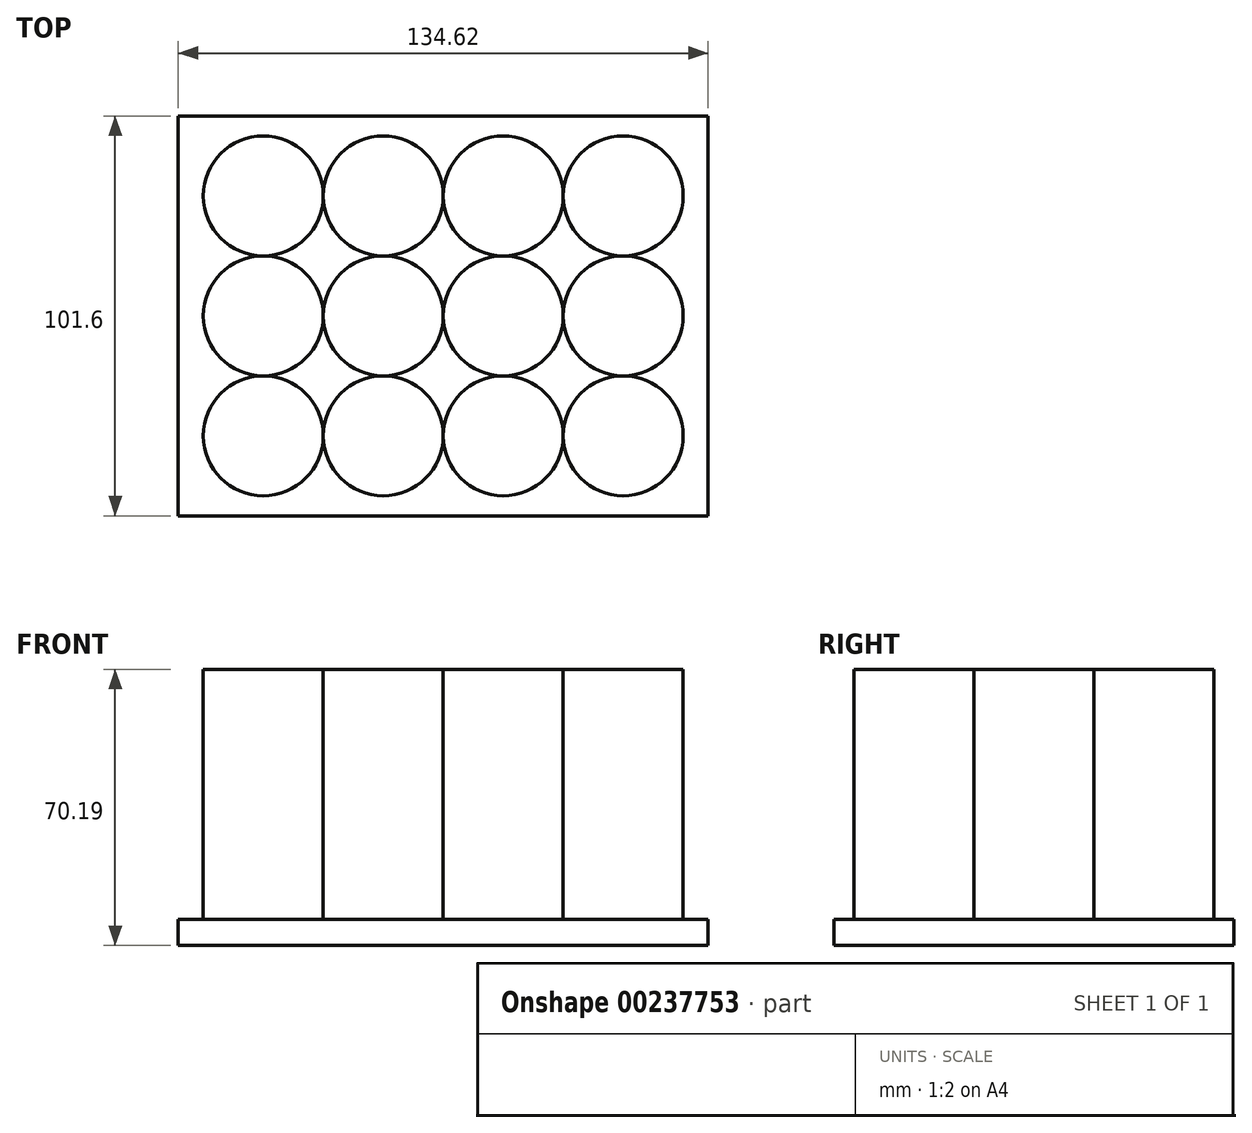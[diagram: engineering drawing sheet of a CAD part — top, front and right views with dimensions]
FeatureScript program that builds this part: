
annotation { "Feature Type Name" : "Feature", "Feature Type Description" : "" }
export const myFeature = defineFeature(function(context is Context, id is Id, definition is map)
    precondition{}
    {
        {
            var Q0;
            Q0=qCreatedBy(makeId("Top.planeOp"),FACE);
            var sketch = newSketch(context, id + "F0", { "sketchPlane" : qUnion([Q0])});
            skCircle(sketch, "E0", {"center": v(-45.72, -30.48) * mm, "radius": 15.24 * mm});
            skCircle(sketch, "E1", {"center": v(-15.24, -30.48) * mm, "radius": 15.24 * mm});
            skCircle(sketch, "E2", {"center": v(15.24, -30.48) * mm, "radius": 15.24 * mm});
            skCircle(sketch, "E3", {"center": v(-45.72, 0) * mm, "radius": 15.24 * mm});
            skCircle(sketch, "E4", {"center": v(-15.24, 0) * mm, "radius": 15.24 * mm});
            skCircle(sketch, "E5", {"center": v(15.24, 0) * mm, "radius": 15.24 * mm});
            skLineSegment(sketch, "E6", {"start": v(-45.72, 0) * mm, "end": v(-45.72, -30.48) * mm, "construction": true});
            skCircle(sketch, "E7", {"center": v(-45.72, 30.48) * mm, "radius": 15.24 * mm});
            skCircle(sketch, "E8", {"center": v(-15.24, 30.48) * mm, "radius": 15.24 * mm});
            skCircle(sketch, "E9", {"center": v(15.24, 30.48) * mm, "radius": 15.24 * mm});
            skLineSegment(sketch, "E10", {"start": v(-45.72, 30.48) * mm, "end": v(-45.72, 0) * mm, "construction": true});
            skCircle(sketch, "E11", {"center": v(45.72, -30.48) * mm, "radius": 15.24 * mm});
            skCircle(sketch, "E12", {"center": v(45.72, 0) * mm, "radius": 15.24 * mm});
            skCircle(sketch, "E13", {"center": v(45.72, 30.48) * mm, "radius": 15.24 * mm});
            skLineSegment(sketch, "E14", {"start": v(45.72, 30.48) * mm, "end": v(45.72, -30.48) * mm, "construction": true});
            skLineSegment(sketch, "E15", {"start": v(-45.72, 0) * mm, "end": v(45.72, 0) * mm, "construction": true});
            skLineSegment(sketch, "E16", {"start": v(-45.72, 30.48) * mm, "end": v(45.72, 30.48) * mm, "construction": true});
            skLineSegment(sketch, "E17", {"start": v(-45.72, -30.48) * mm, "end": v(45.72, -30.48) * mm, "construction": true});
            skSolve(sketch);
        }
        {
            var Q0;
            {var subQ0=sQuery(id+"F0.wireOp",EDGE,"ICpDPUjX-ivMe-23Ei-ieje-qIsjfVPonkm3");var subQ1=makeQuery(id+"F0.imprint","INTERSECT",VERTEX,{"derivedFrom":[subQ0,sQuery(id+"F0.wireOp",EDGE,"1585de0c-b4fc-4455-9636-1ccd38715f07")]});Q0=makeQuery(id+"F0.imprint","IMPRINT",FACE,{"disambiguationData":[TD([[makeQuery(id+"F0.imprint","IMPRINT",EDGE,{"disambiguationData":[TD([[subQ1,-1.0]])],"derivedFrom":subQ0}),1.0]])]});}
            var Q1;
            {var subQ0=sQuery(id+"F0.wireOp",EDGE,"1585de0c-b4fc-4455-9636-1ccd38715f07");var subQ1=makeQuery(id+"F0.imprint","INTERSECT",VERTEX,{"derivedFrom":[sQuery(id+"F0.wireOp",EDGE,"ICpDPUjX-ivMe-23Ei-ieje-qIsjfVPonkm3"),subQ0]});Q1=makeQuery(id+"F0.imprint","IMPRINT",FACE,{"disambiguationData":[TD([[makeQuery(id+"F0.imprint","IMPRINT",EDGE,{"disambiguationData":[TD([[subQ1,1.0]])],"derivedFrom":subQ0}),1.0]])]});}
            var Q2;
            {var subQ0=sQuery(id+"F0.wireOp",EDGE,"8cf919d0-c88a-4376-973f-18324e1bfcb2");var subQ1=makeQuery(id+"F0.imprint","INTERSECT",VERTEX,{"derivedFrom":[sQuery(id+"F0.wireOp",EDGE,"1585de0c-b4fc-4455-9636-1ccd38715f07"),subQ0]});Q2=makeQuery(id+"F0.imprint","IMPRINT",FACE,{"disambiguationData":[TD([[makeQuery(id+"F0.imprint","IMPRINT",EDGE,{"disambiguationData":[TD([[subQ1,-1.0]])],"derivedFrom":subQ0}),1.0]])]});}
            var Q3;
            {var subQ0=sQuery(id+"F0.wireOp",EDGE,"0c448a11-c32a-4d7b-bc3d-f4b18554e8e6");var subQ1=makeQuery(id+"F0.imprint","INTERSECT",VERTEX,{"derivedFrom":[sQuery(id+"F0.wireOp",EDGE,"8cf919d0-c88a-4376-973f-18324e1bfcb2"),subQ0]});Q3=makeQuery(id+"F0.imprint","IMPRINT",FACE,{"disambiguationData":[TD([[makeQuery(id+"F0.imprint","IMPRINT",EDGE,{"disambiguationData":[TD([[subQ1,-1.0]])],"derivedFrom":subQ0}),1.0]])]});}
            var Q4;
            {var subQ0=sQuery(id+"F0.wireOp",EDGE,"877ee094-fdc9-495d-ab0e-c5a52c05f9cd");var subQ4=makeQuery(id+"F0.imprint","INTERSECT",VERTEX,{"derivedFrom":[sQuery(id+"F0.wireOp",EDGE,"8cf919d0-c88a-4376-973f-18324e1bfcb2"),subQ0]});Q4=makeQuery(id+"F0.imprint","IMPRINT",FACE,{"disambiguationData":[TD([[makeQuery(id+"F0.imprint","IMPRINT",EDGE,{"disambiguationData":[TD([[subQ4,1.0]])],"derivedFrom":subQ0}),1.0]])]});}
            var Q5;
            {var subQ0=sQuery(id+"F0.wireOp",EDGE,"d8245553-00ec-417b-91d8-0db8256ae251");var subQ4=makeQuery(id+"F0.imprint","INTERSECT",VERTEX,{"derivedFrom":[sQuery(id+"F0.wireOp",EDGE,"1585de0c-b4fc-4455-9636-1ccd38715f07"),subQ0]});Q5=makeQuery(id+"F0.imprint","IMPRINT",FACE,{"disambiguationData":[TD([[makeQuery(id+"F0.imprint","IMPRINT",EDGE,{"disambiguationData":[TD([[subQ4,1.0]])],"derivedFrom":subQ0}),1.0]])]});}
            var Q6;
            {var subQ0=sQuery(id+"F0.wireOp",EDGE,"E0");var subQ1=makeQuery(id+"F0.imprint","INTERSECT",VERTEX,{"derivedFrom":[sQuery(id+"F0.wireOp",EDGE,"d8245553-00ec-417b-91d8-0db8256ae251"),subQ0]});Q6=makeQuery(id+"F0.imprint","IMPRINT",FACE,{"disambiguationData":[TD([[makeQuery(id+"F0.imprint","IMPRINT",EDGE,{"disambiguationData":[TD([[subQ1,1.0]])],"derivedFrom":subQ0}),1.0]])]});}
            var Q7;
            {var subQ0=sQuery(id+"F0.wireOp",EDGE,"E1");var subQ1=makeQuery(id+"F0.imprint","INTERSECT",VERTEX,{"derivedFrom":[subQ0,sQuery(id+"F0.wireOp",EDGE,"E2")]});Q7=makeQuery(id+"F0.imprint","IMPRINT",FACE,{"disambiguationData":[TD([[makeQuery(id+"F0.imprint","IMPRINT",EDGE,{"disambiguationData":[TD([[subQ1,-1.0]])],"derivedFrom":subQ0}),1.0]])]});}
            var Q8;
            {var subQ0=sQuery(id+"F0.wireOp",EDGE,"E2");var subQ1=makeQuery(id+"F0.imprint","INTERSECT",VERTEX,{"derivedFrom":[sQuery(id+"F0.wireOp",EDGE,"0c448a11-c32a-4d7b-bc3d-f4b18554e8e6"),subQ0]});Q8=makeQuery(id+"F0.imprint","IMPRINT",FACE,{"disambiguationData":[TD([[makeQuery(id+"F0.imprint","IMPRINT",EDGE,{"disambiguationData":[TD([[subQ1,-1.0]])],"derivedFrom":subQ0}),1.0]])]});}
            var Q9;
            {var subQ0=sQuery(id+"F0.wireOp",EDGE,"E3");var subQ1=makeQuery(id+"F0.imprint","INTERSECT",VERTEX,{"derivedFrom":[sQuery(id+"F0.wireOp",EDGE,"E0"),subQ0]});Q9=makeQuery(id+"F0.imprint","IMPRINT",FACE,{"disambiguationData":[TD([[makeQuery(id+"F0.imprint","IMPRINT",EDGE,{"disambiguationData":[TD([[subQ1,1.0]])],"derivedFrom":subQ0}),1.0]])]});}
            var Q10;
            {var subQ0=sQuery(id+"F0.wireOp",EDGE,"E4");var subQ1=makeQuery(id+"F0.imprint","INTERSECT",VERTEX,{"derivedFrom":[sQuery(id+"F0.wireOp",EDGE,"E3"),subQ0]});Q10=makeQuery(id+"F0.imprint","IMPRINT",FACE,{"disambiguationData":[TD([[makeQuery(id+"F0.imprint","IMPRINT",EDGE,{"disambiguationData":[TD([[subQ1,1.0]])],"derivedFrom":subQ0}),1.0]])]});}
            var Q11;
            {var subQ0=sQuery(id+"F0.wireOp",EDGE,"E5");var subQ1=makeQuery(id+"F0.imprint","INTERSECT",VERTEX,{"derivedFrom":[sQuery(id+"F0.wireOp",EDGE,"E2"),subQ0]});Q11=makeQuery(id+"F0.imprint","IMPRINT",FACE,{"disambiguationData":[TD([[makeQuery(id+"F0.imprint","IMPRINT",EDGE,{"disambiguationData":[TD([[subQ1,1.0]])],"derivedFrom":subQ0}),1.0]])]});}
            var Q12;
            Q12=makeQuery(id+"F0.imprint","IMPRINT",FACE,{"disambiguationData":[TD([[makeQuery(id+"F0.imprint","IMPRINT",EDGE,{"derivedFrom":sQuery(id+"F0.wireOp",EDGE,"E13")}),1.0]])]});
            var Q13;
            {var subQ0=sQuery(id+"F0.wireOp",EDGE,"E11");var subQ1=makeQuery(id+"F0.imprint","INTERSECT",VERTEX,{"derivedFrom":[sQuery(id+"F0.wireOp",EDGE,"E2"),subQ0]});Q13=makeQuery(id+"F0.imprint","IMPRINT",FACE,{"disambiguationData":[TD([[makeQuery(id+"F0.imprint","IMPRINT",EDGE,{"disambiguationData":[TD([[subQ1,1.0]])],"derivedFrom":subQ0}),1.0]])]});}
            var Q14;
            {var subQ0=sQuery(id+"F0.wireOp",EDGE,"E8");var subQ1=makeQuery(id+"F0.imprint","INTERSECT",VERTEX,{"derivedFrom":[sQuery(id+"F0.wireOp",EDGE,"E7"),subQ0]});Q14=makeQuery(id+"F0.imprint","IMPRINT",FACE,{"disambiguationData":[TD([[makeQuery(id+"F0.imprint","IMPRINT",EDGE,{"disambiguationData":[TD([[subQ1,1.0]])],"derivedFrom":subQ0}),1.0]])]});}
            var Q15;
            {var subQ0=sQuery(id+"F0.wireOp",EDGE,"E7");var subQ1=makeQuery(id+"F0.imprint","INTERSECT",VERTEX,{"derivedFrom":[sQuery(id+"F0.wireOp",EDGE,"E3"),subQ0]});Q15=makeQuery(id+"F0.imprint","IMPRINT",FACE,{"disambiguationData":[TD([[makeQuery(id+"F0.imprint","IMPRINT",EDGE,{"disambiguationData":[TD([[subQ1,1.0]])],"derivedFrom":subQ0}),1.0]])]});}
            var Q16;
            {var subQ0=sQuery(id+"F0.wireOp",EDGE,"E12");var subQ1=makeQuery(id+"F0.imprint","INTERSECT",VERTEX,{"derivedFrom":[subQ0,sQuery(id+"F0.wireOp",EDGE,"E13")]});Q16=makeQuery(id+"F0.imprint","IMPRINT",FACE,{"disambiguationData":[TD([[makeQuery(id+"F0.imprint","IMPRINT",EDGE,{"disambiguationData":[TD([[subQ1,-1.0]])],"derivedFrom":subQ0}),1.0]])]});}
            var Q17;
            {var subQ0=sQuery(id+"F0.wireOp",EDGE,"E9");var subQ1=makeQuery(id+"F0.imprint","INTERSECT",VERTEX,{"derivedFrom":[sQuery(id+"F0.wireOp",EDGE,"E8"),subQ0]});Q17=makeQuery(id+"F0.imprint","IMPRINT",FACE,{"disambiguationData":[TD([[makeQuery(id+"F0.imprint","IMPRINT",EDGE,{"disambiguationData":[TD([[subQ1,1.0]])],"derivedFrom":subQ0}),1.0]])]});}
            var Q18;
            Q18=sQuery(id+"F0.wireOp",EDGE,"877ee094-fdc9-495d-ab0e-c5a52c05f9cd");
            var Q19;
            Q19=sQuery(id+"F0.wireOp",EDGE,"ICpDPUjX-ivMe-23Ei-ieje-qIsjfVPonkm3");
            var Q20;
            Q20=sQuery(id+"F0.wireOp",EDGE,"E2");
            var Q21;
            Q21=sQuery(id+"F0.wireOp",EDGE,"E1");
            var Q22;
            Q22=sQuery(id+"F0.wireOp",EDGE,"E0");
            var Q23;
            Q23=sQuery(id+"F0.wireOp",EDGE,"0c448a11-c32a-4d7b-bc3d-f4b18554e8e6");
            var Q24;
            Q24=sQuery(id+"F0.wireOp",EDGE,"d8245553-00ec-417b-91d8-0db8256ae251");
            var Q25;
            Q25=sQuery(id+"F0.wireOp",EDGE,"8cf919d0-c88a-4376-973f-18324e1bfcb2");
            var Q26;
            Q26=sQuery(id+"F0.wireOp",EDGE,"1585de0c-b4fc-4455-9636-1ccd38715f07");
            extrude(context, id + "F1", {"entities" : qUnion([Q0, Q1, Q2, Q3, Q4, Q5, Q6, Q7, Q8, Q9, Q10, Q11, Q12, Q13, Q14, Q15, Q16, Q17]), "surfaceEntities" : qUnion([Q18, Q19, Q20, Q21, Q22, Q23, Q24, Q25, Q26]), "depth" : 63.5 * mm});
        }
        {
            var Q0;
            Q0=qCreatedBy(makeId("Front.planeOp"),FACE);
            var sketch = newSketch(context, id + "F2", { "sketchPlane" : qUnion([Q0])});
            skLineSegment(sketch, "E18.bottom", {"start": v(67.31, 0) * mm, "end": v(-67.31, 0) * mm});
            skLineSegment(sketch, "E18.top", {"start": v(67.31, -6.7) * mm, "end": v(-67.31, -6.7) * mm});
            skLineSegment(sketch, "E18.left", {"start": v(67.31, 0) * mm, "end": v(67.31, -6.7) * mm});
            skLineSegment(sketch, "E18.right", {"start": v(-67.31, 0) * mm, "end": v(-67.31, -6.7) * mm});
            skSolve(sketch);
        }
        {
            var Q0;
            Q0=makeQuery(id+"F2.imprint","IMPRINT",FACE,{"disambiguationData":[TD([[makeQuery(id+"F2.imprint","IMPRINT",EDGE,{"derivedFrom":sQuery(id+"F2.wireOp",EDGE,"E18.bottom")}),1.0]])]});
            var Q1;
            Q1=makeQuery(id+"F2.imprint","IMPRINT",FACE,{"disambiguationData":[TD([[makeQuery(id+"F2.imprint","IMPRINT",EDGE,{"derivedFrom":sQuery(id+"F2.wireOp",EDGE,"b8d46107-f48f-4c03-8077-e383a4ff9cb9.bottom")}),1.0]])]});
            var Q2;
            Q2=makeQuery(id+"F2.imprint","IMPRINT",FACE,{"disambiguationData":[TD([[makeQuery(id+"F2.imprint","IMPRINT",EDGE,{"derivedFrom":sQuery(id+"F2.wireOp",EDGE,"8b0a0e72-80e0-4632-a41d-e0e877318674.bottom")}),1.0]])]});
            var Q3;
            Q3=sQuery(id+"F2.wireOp",EDGE,"E18.bottom");
            extrude(context, id + "F3", {"entities" : qUnion([Q0, Q1, Q2]), "surfaceEntities" : qUnion([Q3]), "endBound" : BoundingType.SYMMETRIC, "oppositeDirection" : true, "depth" : 101.6 * mm});
        }
    });
